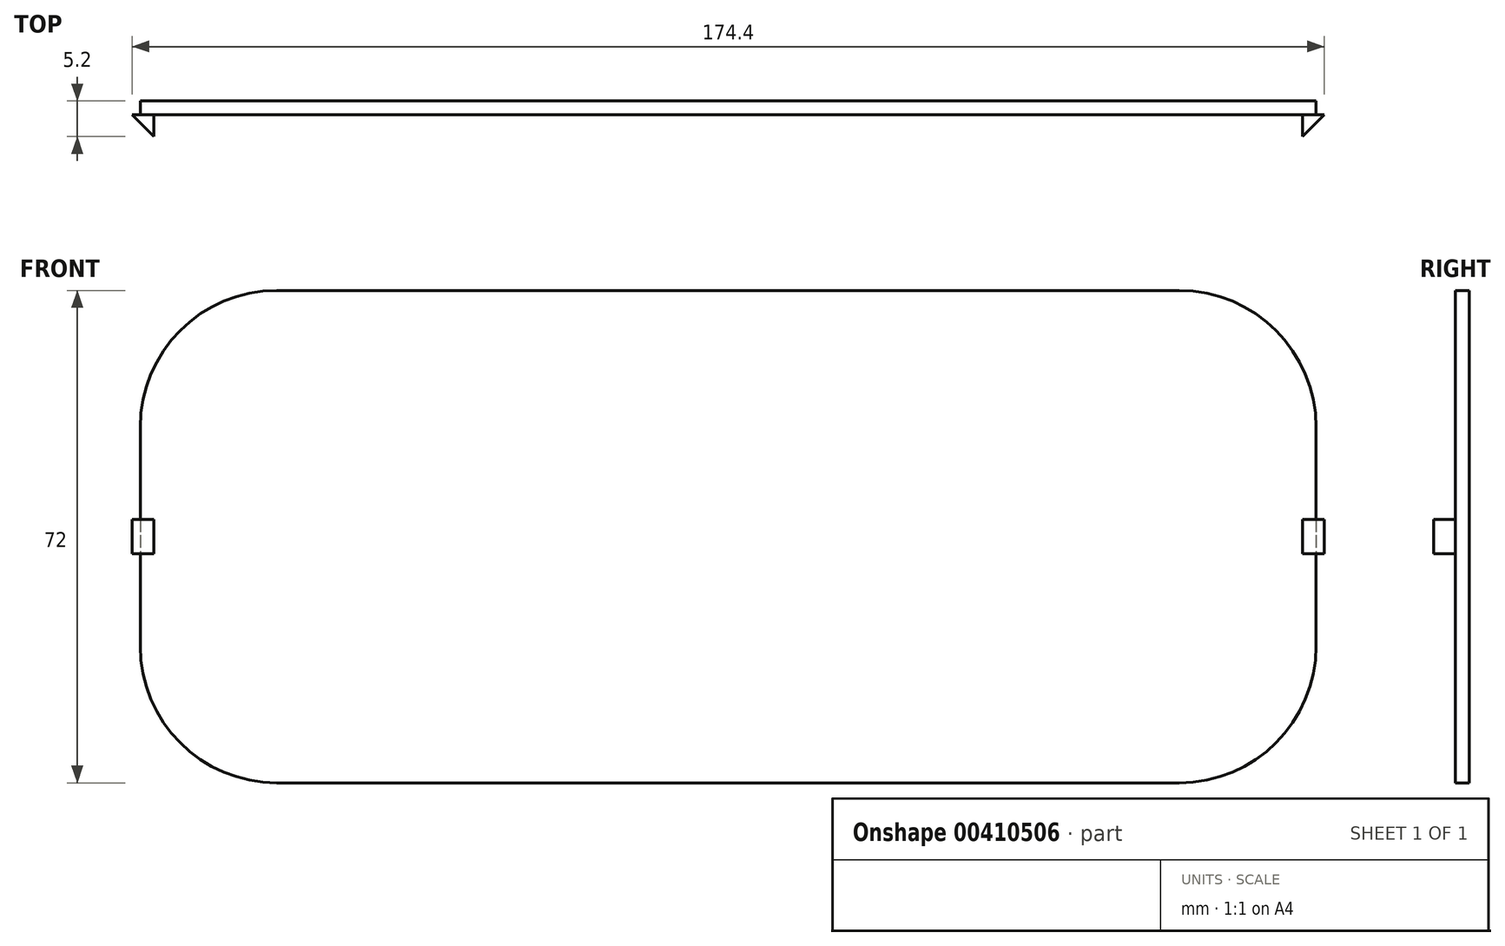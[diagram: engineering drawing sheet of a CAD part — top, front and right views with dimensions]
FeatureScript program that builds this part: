
annotation { "Feature Type Name" : "Feature", "Feature Type Description" : "" }
export const myFeature = defineFeature(function(context is Context, id is Id, definition is map)
    precondition{}
    {
        {
            var Q0;
            Q0=qCreatedBy(makeId("Front.planeOp"),FACE);
            var sketch = newSketch(context, id + "F0", { "sketchPlane" : qUnion([Q0])});
            skLineSegment(sketch, "E0.bottom", {"start": v(66, 36) * mm, "end": v(-66, 36) * mm});
            skLineSegment(sketch, "E0.top", {"start": v(66, -36) * mm, "end": v(-66, -36) * mm});
            skLineSegment(sketch, "E0.left", {"start": v(86, 16) * mm, "end": v(86, -16) * mm});
            skLineSegment(sketch, "E0.right", {"start": v(-86, 16) * mm, "end": v(-86, -16) * mm});
            skPoint(sketch, "E0.middle", {"position": v(0, 0) * mm});
            skPoint(sketch, "E1.visualSharp", {"position": v(86, 36) * mm});
            skArc(sketch, "E1.filletArc", {"start": v(86, 16) * mm, "mid": v(80.14, 30.14) * mm, "end": v(66, 36) * mm});
            skPoint(sketch, "E2.visualSharp", {"position": v(-86, 36) * mm});
            skArc(sketch, "E2.filletArc", {"start": v(-66, 36) * mm, "mid": v(-80.14, 30.14) * mm, "end": v(-86, 16) * mm});
            skPoint(sketch, "E3.visualSharp", {"position": v(-86, -36) * mm});
            skArc(sketch, "E3.filletArc", {"start": v(-86, -16) * mm, "mid": v(-80.14, -30.14) * mm, "end": v(-66, -36) * mm});
            skPoint(sketch, "E4.visualSharp", {"position": v(86, -36) * mm});
            skArc(sketch, "E4.filletArc", {"start": v(66, -36) * mm, "mid": v(80.14, -30.14) * mm, "end": v(86, -16) * mm});
            skLineSegment(sketch, "E5.bottom", {"start": v(84, 2.5) * mm, "end": v(86, 2.5) * mm});
            skLineSegment(sketch, "E5.top", {"start": v(84, -2.5) * mm, "end": v(86, -2.5) * mm});
            skLineSegment(sketch, "E5.left", {"start": v(84, 2.5) * mm, "end": v(84, -2.5) * mm});
            skLineSegment(sketch, "E5.right", {"start": v(86, 2.5) * mm, "end": v(86, -2.5) * mm});
            skLineSegment(sketch, "E6.bottom", {"start": v(-86, 2.5) * mm, "end": v(-84, 2.5) * mm});
            skLineSegment(sketch, "E6.top", {"start": v(-86, -2.5) * mm, "end": v(-84, -2.5) * mm});
            skLineSegment(sketch, "E6.left", {"start": v(-86, 2.5) * mm, "end": v(-86, -2.5) * mm});
            skLineSegment(sketch, "E6.right", {"start": v(-84, 2.5) * mm, "end": v(-84, -2.5) * mm});
            skPoint(sketch, "E7", {"position": v(84, 0) * mm});
            skPoint(sketch, "E8", {"position": v(-84, 0) * mm});
            skSolve(sketch);
        }
        {
            var Q0;
            Q0=makeQuery(id+"F0.imprint","IMPRINT",FACE,{"disambiguationData":[TD([[makeQuery(id+"F0.imprint","IMPRINT",EDGE,{"derivedFrom":sQuery(id+"F0.wireOp",EDGE,"E0.bottom")}),1.0]])]});
            extrude(context, id + "F1", {"entities" : qUnion([Q0]), "depth" : 2 * mm});
        }
        {
            var Q0;
            Q0=makeQuery(id+"F0.imprint","IMPRINT",FACE,{"disambiguationData":[TD([[makeQuery(id+"F0.imprint","IMPRINT",EDGE,{"derivedFrom":sQuery(id+"F0.wireOp",EDGE,"E5.bottom")}),-1.0]])]});
            var Q1;
            Q1=makeQuery(id+"F0.imprint","IMPRINT",FACE,{"disambiguationData":[TD([[makeQuery(id+"F0.imprint","IMPRINT",EDGE,{"derivedFrom":sQuery(id+"F0.wireOp",EDGE,"E6.bottom")}),-1.0]])]});
            extrude(context, id + "F2", {"entities" : qUnion([Q0, Q1]), "operationType" : NewBodyOperationType.ADD, "depth" : 6 * mm});
        }
        {
            var Q0;
            {var subQ0=sQuery(id+"F0.wireOp",EDGE,"E6.left");var subQ1=sQuery(id+"F0.wireOp",EDGE,"E0.right");Q0=makeQuery(id+"F2.boolean.opBoolean","MERGE",FACE,{"derivedFrom":[makeQuery(id+"F1.opExtrude","SWEPT_FACE",FACE,{"disambiguationData":[OSD([subQ1]),TDD([makeQuery(id+"F0.imprint","IMPRINT",EDGE,{"disambiguationData":[TD([[makeQuery(id+"F0.imprint","INTERSECT",VERTEX,{"derivedFrom":[subQ1,sQuery(id+"F0.wireOp",EDGE,"E2.filletArc")]}),-1.0]])],"derivedFrom":subQ1})])]}),makeQuery(id+"F1.opExtrude","SWEPT_FACE",FACE,{"disambiguationData":[OSD([subQ1]),TDD([makeQuery(id+"F0.imprint","IMPRINT",EDGE,{"disambiguationData":[TD([[makeQuery(id+"F0.imprint","INTERSECT",VERTEX,{"derivedFrom":[subQ1,sQuery(id+"F0.wireOp",EDGE,"E3.filletArc")]}),1.0]])],"derivedFrom":subQ1})])]}),makeQuery(id+"F2.opExtrude","SWEPT_FACE",FACE,{"disambiguationData":[OSD([subQ0])]})]});}
            var sketch = newSketch(context, id + "F3", { "sketchPlane" : qUnion([Q0])});
            skLineSegment(sketch, "E9.bottom", {"start": v(6, 2.5) * mm, "end": v(2, 2.5) * mm});
            skLineSegment(sketch, "E9.top", {"start": v(6, -2.5) * mm, "end": v(2, -2.5) * mm});
            skLineSegment(sketch, "E9.left", {"start": v(6, 2.5) * mm, "end": v(6, -2.5) * mm});
            skLineSegment(sketch, "E9.right", {"start": v(2, 2.5) * mm, "end": v(2, -2.5) * mm});
            skSolve(sketch);
        }
        {
            var Q0;
            Q0=makeQuery(id+"F3.imprint","IMPRINT",FACE,{"disambiguationData":[TD([[makeQuery(id+"F3.imprint","IMPRINT",EDGE,{"derivedFrom":sQuery(id+"F3.wireOp",EDGE,"E9.bottom")}),1.0]])]});
            extrude(context, id + "F4", {"entities" : qUnion([Q0]), "operationType" : NewBodyOperationType.ADD, "depth" : 1.2 * mm});
        }
        {
            var Q0;
            {var subQ0=sQuery(id+"F0.wireOp",EDGE,"E5.right");var subQ1=sQuery(id+"F0.wireOp",EDGE,"E0.left");Q0=makeQuery(id+"F2.boolean.opBoolean","MERGE",FACE,{"derivedFrom":[makeQuery(id+"F1.opExtrude","SWEPT_FACE",FACE,{"disambiguationData":[OSD([subQ1]),TDD([makeQuery(id+"F0.imprint","IMPRINT",EDGE,{"disambiguationData":[TD([[makeQuery(id+"F0.imprint","INTERSECT",VERTEX,{"derivedFrom":[subQ1,sQuery(id+"F0.wireOp",EDGE,"E1.filletArc")]}),-1.0]])],"derivedFrom":subQ1})])]}),makeQuery(id+"F1.opExtrude","SWEPT_FACE",FACE,{"disambiguationData":[OSD([subQ1]),TDD([makeQuery(id+"F0.imprint","IMPRINT",EDGE,{"disambiguationData":[TD([[makeQuery(id+"F0.imprint","INTERSECT",VERTEX,{"derivedFrom":[subQ1,sQuery(id+"F0.wireOp",EDGE,"E4.filletArc")]}),1.0]])],"derivedFrom":subQ1})])]}),makeQuery(id+"F2.opExtrude","SWEPT_FACE",FACE,{"disambiguationData":[OSD([subQ0])]})]});}
            var sketch = newSketch(context, id + "F5", { "sketchPlane" : qUnion([Q0])});
            skLineSegment(sketch, "E10.bottom", {"start": v(-6, 2.5) * mm, "end": v(-2, 2.5) * mm});
            skLineSegment(sketch, "E10.top", {"start": v(-6, -2.5) * mm, "end": v(-2, -2.5) * mm});
            skLineSegment(sketch, "E10.left", {"start": v(-6, 2.5) * mm, "end": v(-6, -2.5) * mm});
            skLineSegment(sketch, "E10.right", {"start": v(-2, 2.5) * mm, "end": v(-2, -2.5) * mm});
            skSolve(sketch);
        }
        {
            var Q0;
            Q0=makeQuery(id+"F5.imprint","IMPRINT",FACE,{"disambiguationData":[TD([[makeQuery(id+"F5.imprint","IMPRINT",EDGE,{"derivedFrom":sQuery(id+"F5.wireOp",EDGE,"E10.bottom")}),-1.0]])]});
            extrude(context, id + "F6", {"entities" : qUnion([Q0]), "operationType" : NewBodyOperationType.ADD, "depth" : 1.2 * mm});
        }
        {
            var Q0;
            Q0=makeQuery(id+"F6.opExtrude","CAP_EDGE",EDGE,{"disambiguationData":[OSD([sQuery(id+"F5.wireOp",EDGE,"E10.left")])],"isStart":false});
            var Q1;
            Q1=makeQuery(id+"F4.opExtrude","CAP_EDGE",EDGE,{"disambiguationData":[OSD([sQuery(id+"F3.wireOp",EDGE,"E9.left")])],"isStart":false});
            chamfer(context, id + "F7", {"entities" : qUnion([Q0, Q1]), "width" : 4 * mm, "tangentPropagation" : true});
        }
    });
